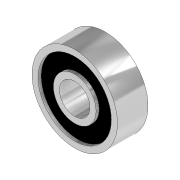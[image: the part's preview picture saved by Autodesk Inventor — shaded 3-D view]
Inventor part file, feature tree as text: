
AUTODESK INVENTOR PART (.ipt)
format: ipt  version: 2020 (Build 240168000, 168)  size: 120,832 bytes
history: native  units: in
note: dims shown in document units (in); Inventor stores cm internally (conversion verified against a paired STEP export)
features: extrude x3, sketch x3, projected_geometry x1
ambient origin geometry x8: Origin, YZ Plane, XZ Plane, XY Plane, X Axis, Y Axis, Z Axis, Center Point
bodies: Solid1 (feature_tree)
feature tree (7):
  extrude  "Extrusion1"  Depth=0.1969in
  extrude  "Extrusion2"  Depth=0.1969in
  extrude  "Extrusion3"  Depth=0.0197in TaperAngle=0.0deg
  sketch  "Sketch1"  dims[d0=0.1969in d1=0.5512in]
  sketch  "Sketch2"  dims[d2=0.1969in d3=0.0in d4=0.0394in]
  projected_geometry  "Projected Loop1"
  sketch  "Sketch3"  dims[d5=0.0394in d6=0.0197in d7=0.0in d8=0.0197in d9=0.0in]
